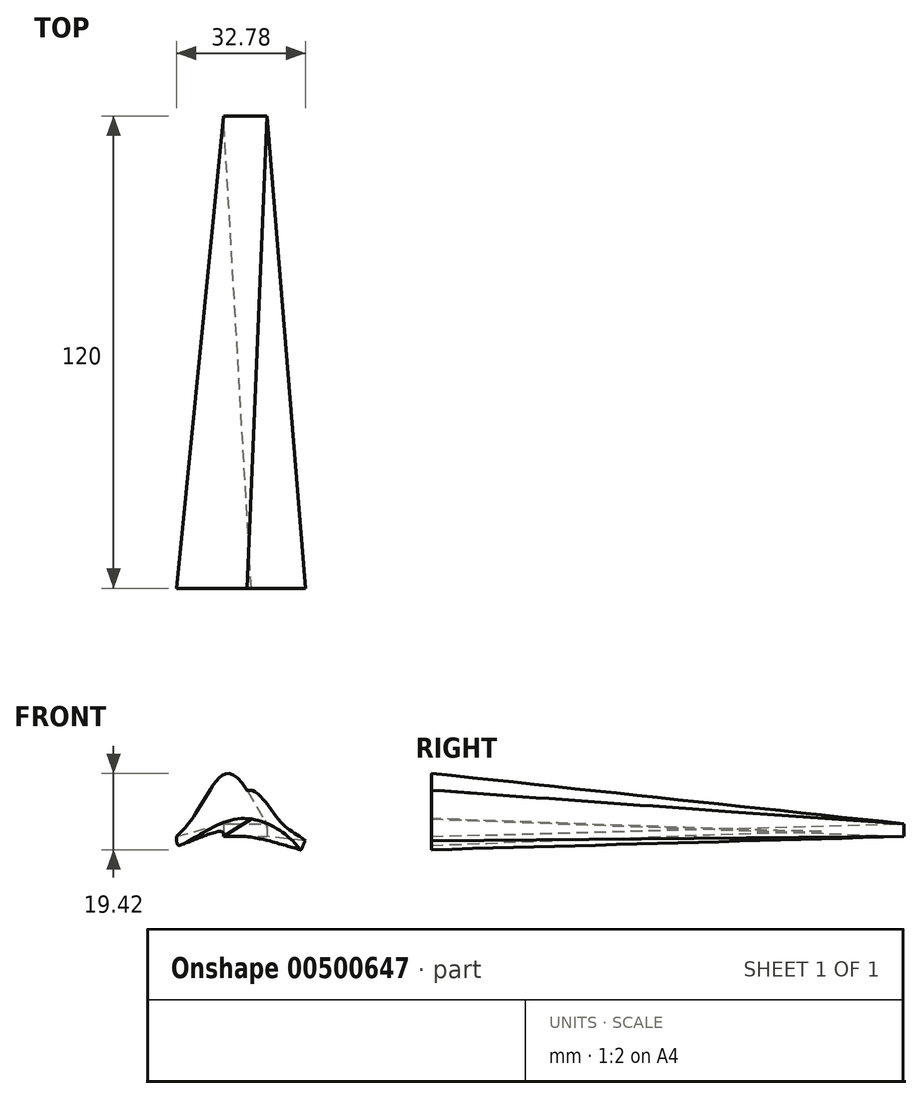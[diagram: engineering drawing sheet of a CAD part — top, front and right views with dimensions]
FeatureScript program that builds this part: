
annotation { "Feature Type Name" : "Feature", "Feature Type Description" : "" }
export const myFeature = defineFeature(function(context is Context, id is Id, definition is map)
    precondition{}
    {
        {
            var Q0;
            Q0=qCreatedBy(makeId("Front.planeOp"),FACE);
            cPlane(context, id + "F0", {"entities" : qUnion([Q0]), "cplaneType" : CPlaneType.OFFSET, "offset" : 60 * mm, "oppositeDirection" : true, "width" : 150 * mm, "height" : 150 * mm});
        }
        {
            var Q0;
            Q0=qCreatedBy(id+"F0.planeOp",FACE);
            cPlane(context, id + "F1", {"entities" : qUnion([Q0]), "cplaneType" : CPlaneType.OFFSET, "offset" : 60 * mm, "oppositeDirection" : true, "width" : 150 * mm, "height" : 150 * mm});
        }
        {
            var Q0;
            Q0=qCreatedBy(makeId("Front.planeOp"),FACE);
            var sketch = newSketch(context, id + "F2", { "sketchPlane" : qUnion([Q0])});
            skFitSpline(sketch, "E0", {"points": [v(0, 11.64) * mm, v(8.01, 4.18) * mm, v(14.8, -1.1) * mm], "startDerivative": vector(15.47, 5.6) * mm, "endDerivative": vector(18.54, -13.9) * mm});
            skFitSpline(sketch, "E1", {"points": [v(0, 11.64) * mm, v(-9.59, 11.64) * mm, v(-18, 0) * mm], "startDerivative": vector(-30.2, 51.12) * mm, "endDerivative": vector(-19.73, -16.64) * mm});
            skFitSpline(sketch, "E2", {"points": [v(-18, 0) * mm, v(-17.43, -2.24) * mm, v(-2.25, 4.47) * mm, v(12.32, -1.95) * mm, v(13.68, -3.38) * mm, v(14.8, -1.1) * mm], "startDerivative": vector(3.1, -25.81) * mm, "endDerivative": vector(15.63, 21.37) * mm});
            skLineSegment(sketch, "E3", {"start": v(0, 17.92) * mm, "end": v(0, -18.05) * mm, "construction": true});
            skLineSegment(sketch, "E4", {"start": v(24.91, 12.56) * mm, "end": v(24.91, -23.7) * mm, "construction": true});
            skSolve(sketch);
        }
        {
            var Q0;
            Q0=qCreatedBy(id+"F1.planeOp",FACE);
            var sketch = newSketch(context, id + "F3", { "sketchPlane" : qUnion([Q0])});
            skLineSegment(sketch, "E5.bottom", {"start": v(-6.02, 3.22) * mm, "end": v(5, 3.22) * mm});
            skLineSegment(sketch, "E5.top", {"start": v(-6.02, 0) * mm, "end": v(5, 0) * mm});
            skLineSegment(sketch, "E5.left", {"start": v(-6.02, 3.22) * mm, "end": v(-6.02, 0) * mm});
            skLineSegment(sketch, "E5.right", {"start": v(5, 3.22) * mm, "end": v(5, 0) * mm});
            skSolve(sketch);
        }
        {
            var Q0;
            Q0=makeQuery(id+"F2.imprint","IMPRINT",FACE,{"disambiguationData":[TD([[makeQuery(id+"F2.imprint","IMPRINT",EDGE,{"derivedFrom":sQuery(id+"F2.wireOp",EDGE,"E0")}),-1.0]])]});
            var Q1;
            Q1=makeQuery(id+"F3.imprint","IMPRINT",FACE,{"disambiguationData":[TD([[makeQuery(id+"F3.imprint","IMPRINT",EDGE,{"derivedFrom":sQuery(id+"F3.wireOp",EDGE,"E5.bottom")}),-1.0]])]});
            loft(context, id + "F4", {"sheetProfilesArray" : [{ "sheetProfileEntities" : qUnion([Q0]) }, { "sheetProfileEntities" : qUnion([Q1]) }]});
        }
    });
